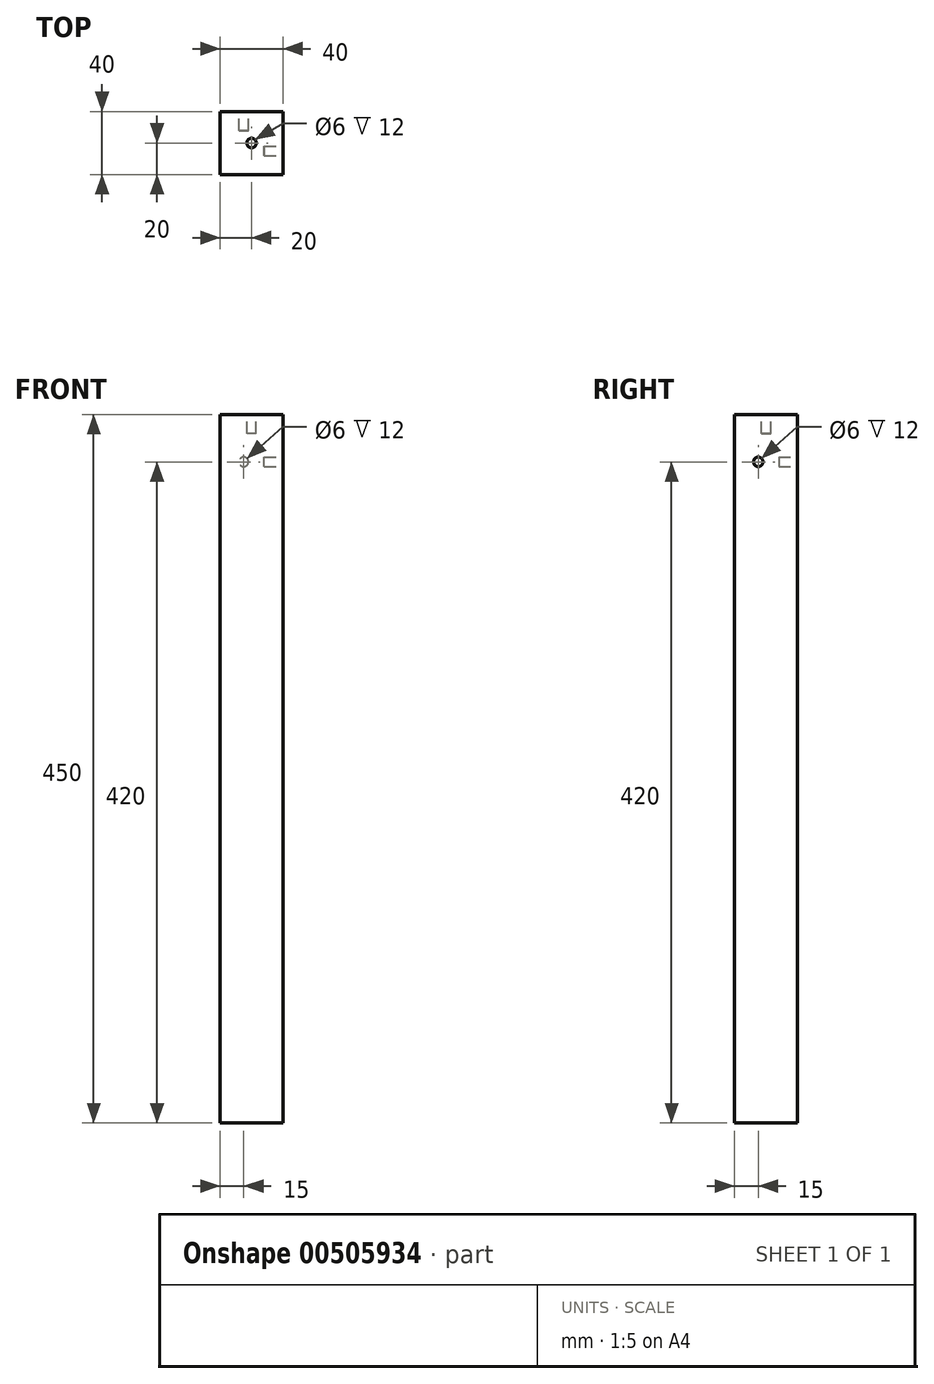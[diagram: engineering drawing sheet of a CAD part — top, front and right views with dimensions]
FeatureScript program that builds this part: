
annotation { "Feature Type Name" : "Feature", "Feature Type Description" : "" }
export const myFeature = defineFeature(function(context is Context, id is Id, definition is map)
    precondition{}
    {
        {
            var Q0;
            Q0=qCreatedBy(makeId("Top.planeOp"),FACE);
            var sketch = newSketch(context, id + "F0", { "sketchPlane" : qUnion([Q0])});
            skLineSegment(sketch, "E0.bottom", {"start": v(0, 0) * mm, "end": v(40, 0) * mm});
            skLineSegment(sketch, "E0.top", {"start": v(0, 40) * mm, "end": v(40, 40) * mm});
            skLineSegment(sketch, "E0.left", {"start": v(0, 0) * mm, "end": v(0, 40) * mm});
            skLineSegment(sketch, "E0.right", {"start": v(40, 0) * mm, "end": v(40, 40) * mm});
            skSolve(sketch);
        }
        {
            var Q0;
            Q0=makeQuery(id+"F0.imprint","IMPRINT",FACE,{"disambiguationData":[TD([[makeQuery(id+"F0.imprint","IMPRINT",EDGE,{"derivedFrom":sQuery(id+"F0.wireOp",EDGE,"E0.bottom")}),1.0]])]});
            extrude(context, id + "F1", {"entities" : qUnion([Q0]), "depth" : 450 * mm, "offsetDistance" : 25 * mm});
        }
        {
            var Q0;
            Q0=makeQuery(id+"F1.opExtrude","CAP_FACE",FACE,{"disambiguationData":[OSD([sQuery(id+"F0.wireOp",EDGE,"E0.bottom"),sQuery(id+"F0.wireOp",EDGE,"E0.top"),sQuery(id+"F0.wireOp",EDGE,"E0.left"),sQuery(id+"F0.wireOp",EDGE,"E0.right")])],"isStart":false});
            var sketch = newSketch(context, id + "F2", { "sketchPlane" : qUnion([Q0])});
            skSolve(sketch);
        }
        {
            var Q0;
            Q0=makeQuery(id+"F1.opExtrude","SWEPT_FACE",FACE,{"disambiguationData":[OSD([sQuery(id+"F0.wireOp",EDGE,"E0.right")])]});
            var sketch = newSketch(context, id + "F3", { "sketchPlane" : qUnion([Q0])});
            skCircle(sketch, "E1", {"center": v(15, 420) * mm, "radius": 3 * mm});
            skSolve(sketch);
        }
        {
            var Q0;
            Q0=makeQuery(id+"F3.imprint","IMPRINT",FACE,{"disambiguationData":[TD([[makeQuery(id+"F3.imprint","IMPRINT",EDGE,{"derivedFrom":sQuery(id+"F3.wireOp",EDGE,"E1")}),1.0]])]});
            extrude(context, id + "F4", {"entities" : qUnion([Q0]), "operationType" : NewBodyOperationType.REMOVE, "oppositeDirection" : true, "depth" : 12 * mm});
        }
        {
            var Q0;
            Q0=makeQuery(id+"F1.opExtrude","SWEPT_FACE",FACE,{"disambiguationData":[OSD([sQuery(id+"F0.wireOp",EDGE,"E0.top")])]});
            var sketch = newSketch(context, id + "F5", { "sketchPlane" : qUnion([Q0])});
            skCircle(sketch, "E2", {"center": v(-15, 420) * mm, "radius": 3 * mm});
            skSolve(sketch);
        }
        {
            var Q0;
            Q0=makeQuery(id+"F5.imprint","IMPRINT",FACE,{"disambiguationData":[TD([[makeQuery(id+"F5.imprint","IMPRINT",EDGE,{"derivedFrom":sQuery(id+"F5.wireOp",EDGE,"E2")}),1.0]])]});
            extrude(context, id + "F6", {"entities" : qUnion([Q0]), "operationType" : NewBodyOperationType.REMOVE, "oppositeDirection" : true, "depth" : 12 * mm});
        }
        {
            var Q0;
            Q0=makeQuery(id+"F2.imprint","IMPRINT",FACE,{"disambiguationData":[TD([[makeQuery(id+"F2.imprint","IMPRINT",EDGE,{"derivedFrom":makeQuery(id+"F1.opExtrude","CAP_EDGE",EDGE,{"disambiguationData":[OSD([sQuery(id+"F0.wireOp",EDGE,"E0.bottom")])],"isStart":false})}),1.0]])]});
            var sketch = newSketch(context, id + "F7", { "sketchPlane" : qUnion([Q0])});
            skCircle(sketch, "E3", {"center": v(20, 20) * mm, "radius": 3 * mm});
            skSolve(sketch);
        }
        {
            var Q0;
            Q0=makeQuery(id+"F7.imprint","IMPRINT",FACE,{"disambiguationData":[TD([[makeQuery(id+"F7.imprint","IMPRINT",EDGE,{"derivedFrom":sQuery(id+"F7.wireOp",EDGE,"E3")}),1.0]])]});
            extrude(context, id + "F8", {"entities" : qUnion([Q0]), "operationType" : NewBodyOperationType.REMOVE, "oppositeDirection" : true, "depth" : 12 * mm, "offsetDistance" : 25 * mm});
        }
    });
